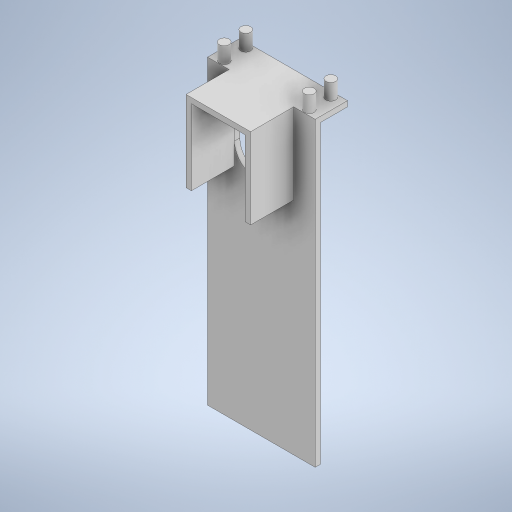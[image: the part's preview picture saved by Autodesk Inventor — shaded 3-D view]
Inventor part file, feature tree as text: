
AUTODESK INVENTOR PART (.ipt)
format: ipt  version: 2023 (Build 270158000, 158)  size: 315,904 bytes
history: native  units: mm
features: extrude x7, sketch x7
ambient origin geometry x8: Origin, YZ Plane, XZ Plane, XY Plane, X Axis, Y Axis, Z Axis, Center Point
bodies: Solid1 (feature_tree)
feature tree (14):
  extrude  "Extrusion1"  Depth=100.0mm
  extrude  "Extrusion6"  Depth=50.0mm
  sketch  "Sketch15"  dims[d22=50.0mm d23=20.0mm]
  sketch  "Sketch16"  dims[d24=5.0mm d25=0.0mm d46=100.0mm]
  extrude  "Extrusion11"  Depth=20.0mm
  extrude  "Extrusion12"  Depth=100.0mm
  extrude  "Extrusion17"  Depth=30.0mm
  extrude  "Extrusion18"  Depth=9.0mm
  extrude  "Extrusion19"  Depth=5.0mm TaperAngle=0.0deg
  sketch  "Sketch1"  dims[d0=100.0mm d1=200.0mm]
  sketch  "Sketch6"  dims[d2=5.0mm d3=0.0mm d21=50.0mm]
  sketch  "Sketch21"  dims[d47=30.0mm d48=9.0mm]
  sketch  "Sketch23"  dims[d49=9.0mm d50=9.0mm]
  sketch  "Sketch24"  dims[d51=9.0mm d52=5.0mm d53=0.0mm d54=15.0mm d55=0.0mm d66=100.0mm d67=80.0mm d68=5.0mm d69=0.0mm d72=60.0mm d73=75.0mm d74=40.0mm d75=0.0mm d76=50.0mm d77=40.0mm d78=0.0mm]
